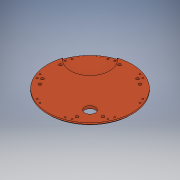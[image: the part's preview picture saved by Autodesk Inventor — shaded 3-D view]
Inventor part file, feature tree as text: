
AUTODESK INVENTOR PART (.ipt)
format: ipt  version: 2018 (Build 220112000, 112)  size: 204,288 bytes
history: native  units: in
note: dims shown in document units (in); Inventor stores cm internally (conversion verified against a paired STEP export)
features: sketch x7, extrude x4, hole x3, pattern_circular x1
ambient origin geometry x8: Origin, YZ Plane, XZ Plane, XY Plane, X Axis, Y Axis, Z Axis, Center Point
bodies: Solid1 (feature_tree)
feature tree (15):
  extrude  "Extrusion1"  Depth=0.25in TaperAngle=0.0deg
  hole  "Hole2"  [1 undecoded]
  pattern_circular  "Circular Pattern2"  Count=8 Angle=360.0deg
  extrude  "Extrusion4"  Depth=4.0in
  sketch  "Sketch8"  dims[d31=7.75in d33=0.0in d34=0.125in d39=4.0in]
  hole  "Hole3"  [1 undecoded]
  extrude  "Extrusion6"  Depth=0.25in
  hole  "Hole5"  [1 undecoded]
  sketch  "Sketch1"  dims[d0=8.0in d1=0.25in d2=0.0in]
  sketch  "Sketch3"  dims[d14=3.75in d15=22.5deg]
  sketch  "Sketch6"  dims[d17=90.0deg]
  sketch  "Sketch7"  dims[d18=0.15in d19=0.224in d20=0.225in d21=0.25in d22=0.5635in d23=0.349in d24=0.8108in d25=3.1496in d26=360.0deg]
  sketch  "Sketch11"  dims[d40=45.0deg d41=1.5in d42=1.0in d43=1.0in d44=0.0in d45=2.5in d46=3.81in d47=135.0deg d48=11.0in d49=5.5in d50=1.9354in d56=6.6in d57=0.266in d58=0.75in d59=0.507in d60=0.25in d61=0.5635in d62=1.0in d63=0.8108in d64=5.85in d65=135.0deg d66=3.7in d69=0.1in d70=0.0in d109=135.0deg d110=3.767in d111=6.8in d112=0.3086in d113=0.8027in d114=0.0206in d115=10.0in d116=0.0206in d117=5.1in d118=5.2in d119=0.266in d120=0.75in d121=0.507in d122=0.25in d123=0.5635in d124=1.0in d125=0.8108in]
  sketch  "Sketch5"  dims[d16=0.25in]
  extrude  "Extrusion3"  Depth=0.25in
note: 3 required parameter values undecoded (feature->parameter linkage not recoverable at this tier; creation-order binding heuristic only, values carry confidence <= 0.55)
